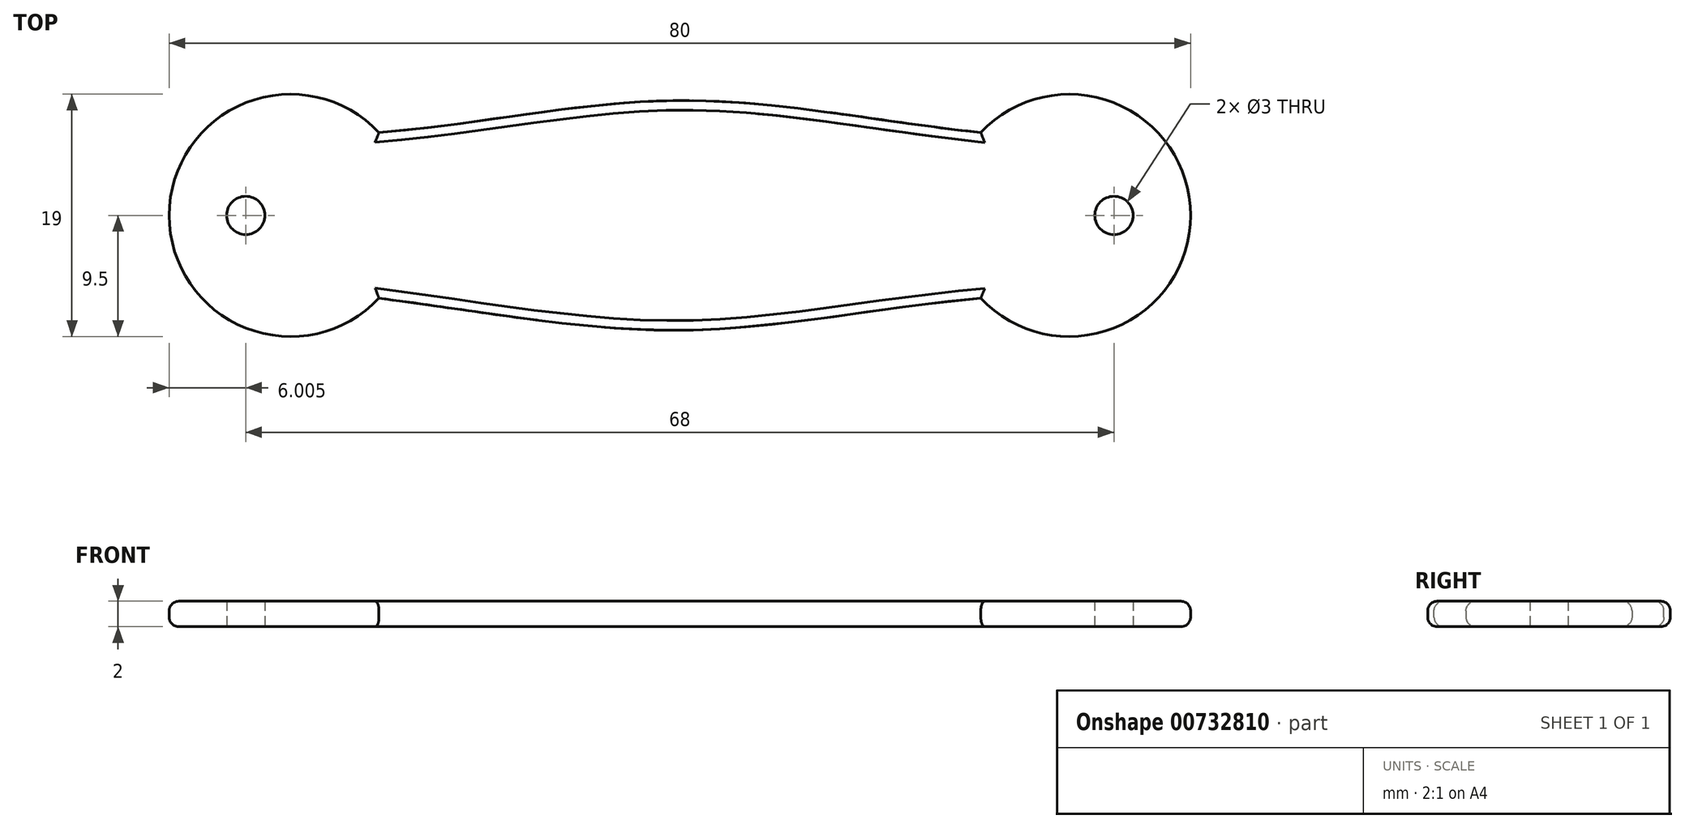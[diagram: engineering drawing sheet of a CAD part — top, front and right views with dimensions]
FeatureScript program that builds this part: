
annotation { "Feature Type Name" : "Feature", "Feature Type Description" : "" }
export const myFeature = defineFeature(function(context is Context, id is Id, definition is map)
    precondition{}
    {
        {
            var Q0;
            Q0=qCreatedBy(makeId("Top.planeOp"),FACE);
            var sketch = newSketch(context, id + "F0", { "sketchPlane" : qUnion([Q0])});
            skCircle(sketch, "E0", {"center": v(-42.46, 0) * mm, "radius": 9.5 * mm});
            skCircle(sketch, "E1", {"center": v(18.54, 0) * mm, "radius": 9.5 * mm});
            skCircle(sketch, "E2", {"center": v(-45.96, 0) * mm, "radius": 1.5 * mm});
            skCircle(sketch, "E3", {"center": v(22.04, 0) * mm, "radius": 1.5 * mm});
            skPoint(sketch, "E4.1.internal.snap0", {"position": v(-11.96, -9.5) * mm});
            skFitSpline(sketch, "E4", {"points": [v(-35.53, -6.5) * mm, v(-11.96, -9) * mm, v(11.62, -6.5) * mm], "startDerivative": vector(47, -5.8) * mm, "endDerivative": vector(48.36, 4.16) * mm});
            skPoint(sketch, "E5.1.internal.snap0", {"position": v(-11.96, 9.5) * mm});
            skFitSpline(sketch, "E5", {"points": [v(-35.53, 6.5) * mm, v(-11.96, 9) * mm, v(11.62, 6.5) * mm], "startDerivative": vector(48.34, 3.85) * mm, "endDerivative": vector(47.47, -4.87) * mm});
            skPoint(sketch, "E6.orphan", {"position": v(-42.46, 9.5) * mm});
            skPoint(sketch, "E7.end.orphan", {"position": v(18.54, 9.5) * mm});
            skPoint(sketch, "E8.orphan", {"position": v(18.54, -9.5) * mm});
            skPoint(sketch, "E9.start.orphan", {"position": v(-42.46, -9.5) * mm});
            skSolve(sketch);
        }
        {
            var Q0;
            Q0 = qSketchRegion(id + "F0", true);
            extrude(context, id + "F1", {"entities" : qUnion([Q0]), "depth" : 2 * mm, "offsetDistance" : 25 * mm});
        }
        {
            var Q0;
            Q0=makeQuery(id+"F1.opExtrude","CAP_EDGE",EDGE,{"disambiguationData":[OSD([sQuery(id+"F0.wireOp",EDGE,"E4")])],"isStart":true});
            var Q1;
            Q1=makeQuery(id+"F1.opExtrude","CAP_EDGE",EDGE,{"disambiguationData":[OSD([sQuery(id+"F0.wireOp",EDGE,"E4")])],"isStart":false});
            var Q2;
            Q2=makeQuery(id+"F1.opExtrude","CAP_EDGE",EDGE,{"disambiguationData":[OSD([sQuery(id+"F0.wireOp",EDGE,"E0")])],"isStart":false});
            var Q3;
            Q3=makeQuery(id+"F1.opExtrude","CAP_EDGE",EDGE,{"disambiguationData":[OSD([sQuery(id+"F0.wireOp",EDGE,"E0")])],"isStart":true});
            var Q4;
            Q4=makeQuery(id+"F1.opExtrude","CAP_EDGE",EDGE,{"disambiguationData":[OSD([sQuery(id+"F0.wireOp",EDGE,"E5")])],"isStart":false});
            var Q5;
            Q5=makeQuery(id+"F1.opExtrude","CAP_EDGE",EDGE,{"disambiguationData":[OSD([sQuery(id+"F0.wireOp",EDGE,"E1")])],"isStart":false});
            var Q6;
            Q6=makeQuery(id+"F1.opExtrude","CAP_EDGE",EDGE,{"disambiguationData":[OSD([sQuery(id+"F0.wireOp",EDGE,"E1")])],"isStart":true});
            var Q7;
            Q7=makeQuery(id+"F1.opExtrude","CAP_EDGE",EDGE,{"disambiguationData":[OSD([sQuery(id+"F0.wireOp",EDGE,"E5")])],"isStart":true});
            fillet(context, id + "F2", {"entities" : qUnion([Q0, Q1, Q2, Q3, Q4, Q5, Q6, Q7]), "radius" : .75 * mm, "tangentPropagation" : true, "allowEdgeOverflow" : false});
        }
    });
